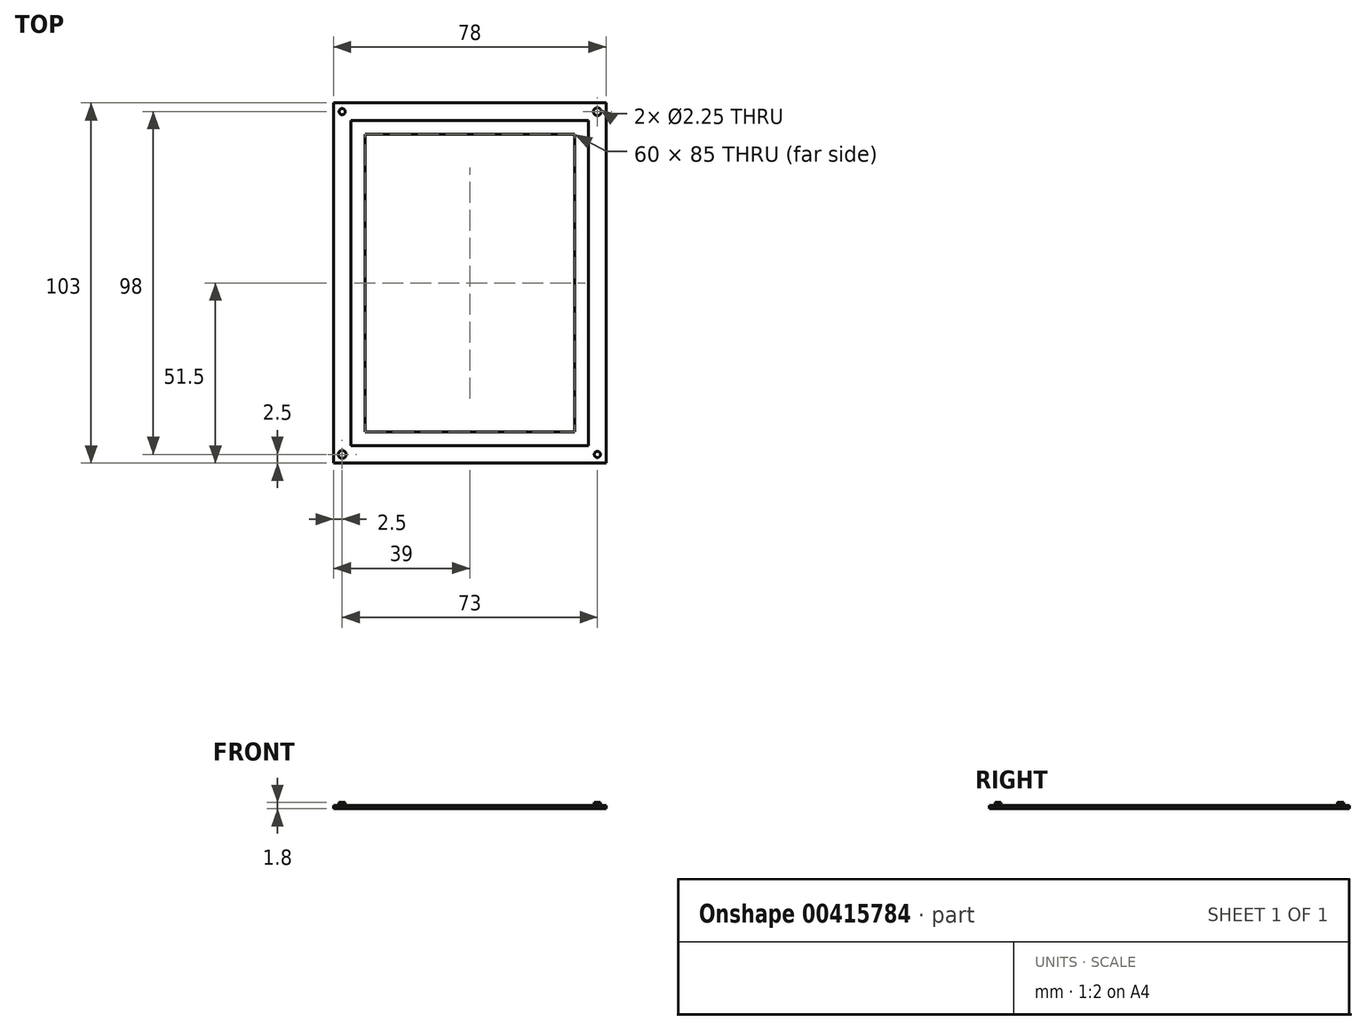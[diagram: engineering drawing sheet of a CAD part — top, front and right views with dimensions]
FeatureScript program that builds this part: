
annotation { "Feature Type Name" : "Feature", "Feature Type Description" : "" }
export const myFeature = defineFeature(function(context is Context, id is Id, definition is map)
    precondition{}
    {
        {
            var Q0;
            Q0=qCreatedBy(makeId("Top.planeOp"),FACE);
            var sketch = newSketch(context, id + "F0", { "sketchPlane" : qUnion([Q0])});
            skLineSegment(sketch, "E0.bottom", {"start": v(0, 0) * mm, "end": v(78, 0) * mm});
            skLineSegment(sketch, "E0.top", {"start": v(0, 103) * mm, "end": v(78, 103) * mm});
            skLineSegment(sketch, "E0.left", {"start": v(0, 0) * mm, "end": v(0, 103) * mm});
            skLineSegment(sketch, "E0.right", {"start": v(78, 0) * mm, "end": v(78, 103) * mm});
            skLineSegment(sketch, "E1.bottom", {"start": v(5, 5) * mm, "end": v(73, 5) * mm});
            skLineSegment(sketch, "E1.top", {"start": v(5, 98) * mm, "end": v(73, 98) * mm});
            skLineSegment(sketch, "E1.left", {"start": v(5, 5) * mm, "end": v(5, 98) * mm});
            skLineSegment(sketch, "E1.right", {"start": v(73, 5) * mm, "end": v(73, 98) * mm});
            skLineSegment(sketch, "E2.bottom", {"start": v(9, 9) * mm, "end": v(69, 9) * mm});
            skLineSegment(sketch, "E2.top", {"start": v(9, 94) * mm, "end": v(69, 94) * mm});
            skLineSegment(sketch, "E2.left", {"start": v(9, 9) * mm, "end": v(9, 94) * mm});
            skLineSegment(sketch, "E2.right", {"start": v(69, 9) * mm, "end": v(69, 94) * mm});
            skCircle(sketch, "E3", {"center": v(2.5, 100.5) * mm, "radius": 0.88 * mm});
            skCircle(sketch, "E4", {"center": v(75.5, 100.5) * mm, "radius": 1.13 * mm});
            skCircle(sketch, "E5", {"center": v(75.5, 2.5) * mm, "radius": 0.87 * mm});
            skCircle(sketch, "E6", {"center": v(2.5, 2.5) * mm, "radius": 1.13 * mm});
            skSolve(sketch);
        }
        {
            var Q0;
            Q0=makeQuery(id+"F0.imprint","IMPRINT",FACE,{"disambiguationData":[TD([[makeQuery(id+"F0.imprint","IMPRINT",EDGE,{"derivedFrom":sQuery(id+"F0.wireOp",EDGE,"E1.bottom")}),1.0]])]});
            extrude(context, id + "F1", {"entities" : qUnion([Q0]), "depth" : .5 * mm});
        }
        {
            var Q0;
            Q0 = qSketchRegion(id + "F0", true);
            extrude(context, id + "F2", {"entities" : qUnion([Q0]), "operationType" : NewBodyOperationType.ADD, "depth" : 1 * mm});
        }
        {
            var Q0;
            Q0=makeQuery(id+"F0.imprint","IMPRINT",FACE,{"disambiguationData":[TD([[makeQuery(id+"F0.imprint","IMPRINT",EDGE,{"derivedFrom":sQuery(id+"F0.wireOp",EDGE,"E5")}),1.0]])]});
            var Q1;
            Q1=makeQuery(id+"F0.imprint","IMPRINT",FACE,{"disambiguationData":[TD([[makeQuery(id+"F0.imprint","IMPRINT",EDGE,{"derivedFrom":sQuery(id+"F0.wireOp",EDGE,"E3")}),1.0]])]});
            extrude(context, id + "F3", {"entities" : qUnion([Q0, Q1]), "operationType" : NewBodyOperationType.ADD, "depth" : 1.8 * mm});
        }
    });
